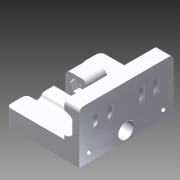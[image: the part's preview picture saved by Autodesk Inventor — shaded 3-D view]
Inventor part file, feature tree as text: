
AUTODESK INVENTOR PART (.ipt)
format: ipt  version: 2015 SP1 (Build 190203100, 203)  size: 499,200 bytes
history: native  units: mm
features: sketch x21, extrude x18, projected_geometry x10, fillet x9, reference x7, hole x2, mirror x1, plane x1, other x1, revolve x1
ambient origin geometry x8: Origin, YZ Plane, XZ Plane, XY Plane, X Axis, Y Axis, Z Axis, Center Point
bodies: Solid1 (feature_tree)
feature tree (71):
  extrude  "Extrusion1"  Depth=12.0mm
  extrude  "Extrusion2"  Depth=10.0mm
  extrude  "Extrusion3"  Depth=25.0mm TaperAngle=0.0deg
  extrude  "Extrusion4"  Depth=16.0mm TaperAngle=0.0deg
  extrude  "Extrusion5"  Depth=24.0mm TaperAngle=0.0deg
  extrude  "Extrusion6"  Depth=2.0mm
  extrude  "Extrusion7"  Depth=4.0mm
  mirror  "Mirror1"
  plane  "Work Plane1"
  extrude  "Extrusion9"  Depth=4.0mm
  sketch  "Sketch8"  dims[d19=4.0mm d20=4.0mm]
  other  "Work Axis1"
  revolve  "Revolution1"  [1 undecoded]
  fillet  "Fillet9"  Radius=2.0mm
  fillet  "Fillet11"  Radius=1.75mm
  extrude  "Extrusion18"  Depth=10.0mm TaperAngle=0.0deg
  extrude  "Extrusion19"  Depth=1.75mm
  extrude  "Extrusion20"  Depth=10.0mm TaperAngle=0.0deg
  fillet  "Fillet13"  Radius=5.0mm
  fillet  "Fillet12"  Radius=5.0mm
  extrude  "Extrusion21"  Depth=1.5mm
  extrude  "Extrusion22"  Depth=10.0mm
  extrude  "Extrusion23"  Depth=22.2mm
  extrude  "Extrusion24"  Depth=10.5mm
  fillet  "Fillet15"  Radius=8.0mm
  fillet  "Fillet16"  Radius=2.0mm
  fillet  "Fillet17"  Radius=0.75mm
  fillet  "Fillet18"  Radius=18.0mm
  hole  "Hole1"  [1 undecoded]
  extrude  "Extrusion25"  Depth=17.0mm TaperAngle=0.0deg
  extrude  "Extrusion26"  Depth=4.5mm TaperAngle=0.0deg
  fillet  "Fillet19"  Radius=2.0mm
  extrude  "Extrusion - extend smooth rod hole"  Depth=4.0mm
  hole  "Hole2"  [1 undecoded]
  sketch  "Sketch1"  dims[d0=66.0mm d1=12.0mm]
  sketch  "Sketch2"  dims[d2=10.0mm d3=0.0mm d4=14.0mm]
  sketch  "Sketch3"  dims[d5=14.0mm d6=25.0mm d7=0.0mm]
  reference  "Reference1"
  reference  "Reference2"
  sketch  "Sketch4"  dims[d8=25.0mm d9=0.0mm d10=16.0mm d11=0.0mm]
  projected_geometry  "Projected Loop1"
  sketch  "Sketch6"  dims[d13=10.5mm d14=24.0mm d15=0.0mm]
  sketch  "Sketch7"  dims[d16=20.0mm d17=0.0mm d18=2.0mm]
  reference  "Reference4"
  sketch  "Sketch9"  dims[d21=4.0mm d22=4.0mm]
  sketch  "Sketch11"  dims[d23=6.0mm d24=6.0mm d25=2.0mm d26=1.75mm]
  sketch  "Sketch17"  dims[d27=10.0mm d28=5.0mm d29=0.0mm]
  sketch  "Sketch20"  dims[d30=-29.0mm d35=1.75mm]
  sketch  "Sketch21"  dims[d36=10.0mm d37=8.0mm d38=0.0mm d39=5.0mm d40=5.0mm]
  projected_geometry  "Projected Loop3"
  sketch  "Sketch22"  dims[d41=90.0deg d71=1.5mm]
  projected_geometry  "Projected Loop4"
  projected_geometry  "Projected Loop5"
  sketch  "Sketch23"  dims[d73=3.0mm d76=10.0mm]
  projected_geometry  "Projected Loop6"
  sketch  "Sketch25"  dims[d84=18.0mm d85=0.0mm d86=22.2mm]
  projected_geometry  "Projected Loop8"
  sketch  "Sketch26"  dims[d87=8.0mm d88=0.0mm d89=10.5mm d90=8.0mm d91=0.0mm d92=2.0mm d93=0.75mm d94=18.0mm d95=0.0mm]
  reference  "Reference7"
  sketch  "Sketch27"  dims[d97=18.0mm d98=0.0mm d99=15.5mm]
  reference  "Reference8"
  sketch  "Sketch28"  dims[d100=14.0mm d101=17.0mm d102=0.0mm]
  projected_geometry  "Projected Loop9"
  sketch  "Sketch29"  dims[d103=7.9mm d104=4.5mm d105=0.0mm d106=2.0mm]
  projected_geometry  "Projected Loop10"
  sketch  "Sketch30"  dims[d107=3.0mm d108=4.0mm]
  projected_geometry  "Projected Loop11"
  projected_geometry  "Projected Loop12"
  sketch  "Sketch31"  dims[d109=10.0mm d110=6.0mm d111=6.0mm d112=4.0mm d113=2.0mm d114=90.0deg d115=8.0mm d116=20.594885mm d117=1.0mm d118=0.0mm d119=1.0mm d120=0.0mm d121=2.0mm d122=10.0mm d123=0.0mm d124=3.0mm d125=6.0mm d126=4.0mm d127=2.0mm d128=90.0deg d129=8.0mm d130=20.594885mm]
  reference  "Reference9"
  reference  "Reference10"
note: 3 required parameter values undecoded (feature->parameter linkage not recoverable at this tier; creation-order binding heuristic only, values carry confidence <= 0.55)